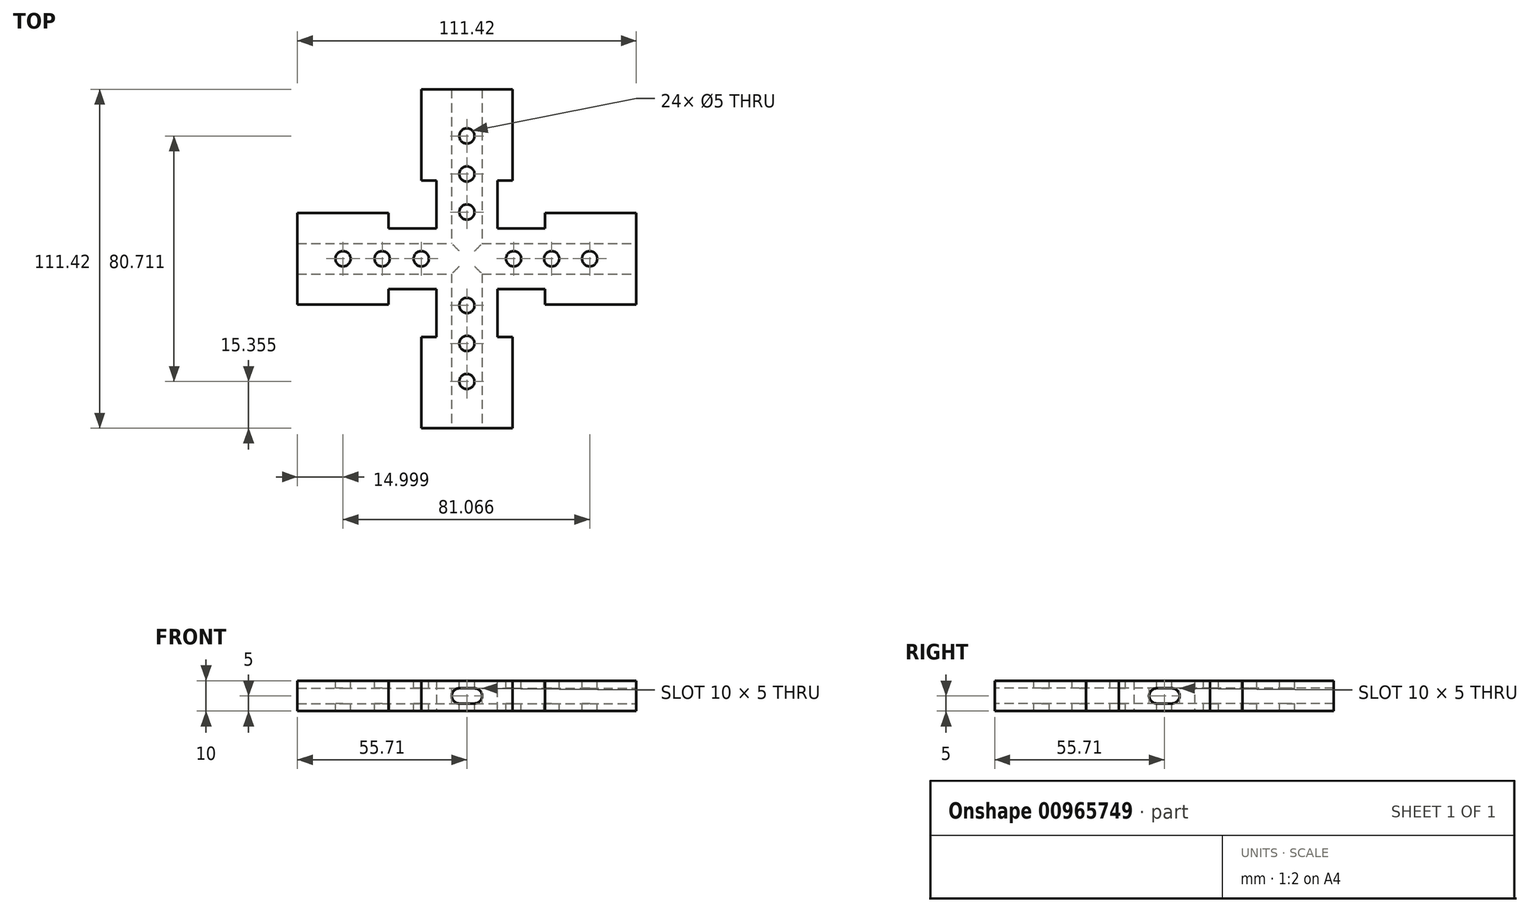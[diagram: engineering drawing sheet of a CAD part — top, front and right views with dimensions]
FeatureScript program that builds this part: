
annotation { "Feature Type Name" : "Feature", "Feature Type Description" : "" }
export const myFeature = defineFeature(function(context is Context, id is Id, definition is map)
    precondition{}
    {
        {
            var Q0;
            Q0=qCreatedBy(makeId("Top.planeOp"),FACE);
            var sketch = newSketch(context, id + "F0", { "sketchPlane" : qUnion([Q0])});
            skLineSegment(sketch, "E0.bottom", {"start": v(55.71, 10) * mm, "end": v(-55.71, 10) * mm});
            skLineSegment(sketch, "E0.top", {"start": v(55.71, -10) * mm, "end": v(-55.71, -10) * mm});
            skLineSegment(sketch, "E0.left", {"start": v(55.71, 10) * mm, "end": v(55.71, -10) * mm});
            skLineSegment(sketch, "E0.right", {"start": v(-55.71, 10) * mm, "end": v(-55.71, -10) * mm});
            skPoint(sketch, "E0.middle", {"position": v(0, 0) * mm});
            skLineSegment(sketch, "E1.bottom", {"start": v(10, 55.71) * mm, "end": v(-10, 55.71) * mm});
            skLineSegment(sketch, "E1.top", {"start": v(10, -55.71) * mm, "end": v(-10, -55.71) * mm});
            skLineSegment(sketch, "E1.left", {"start": v(10, 55.71) * mm, "end": v(10, -55.71) * mm});
            skLineSegment(sketch, "E1.right", {"start": v(-10, 55.71) * mm, "end": v(-10, -55.71) * mm});
            skSolve(sketch);
        }
        {
            var Q0;
            Q0 = qSketchRegion(id + "F0", true);
            extrude(context, id + "F1", {"entities" : qUnion([Q0]), "endBound" : BoundingType.SYMMETRIC, "depth" : 10 * mm, "offsetDistance" : 25 * mm});
        }
        {
            var Q0;
            Q0=makeQuery(id+"F1.opExtrude","SWEPT_FACE",FACE,{"disambiguationData":[OSD([sQuery(id+"F0.wireOp",EDGE,"E1.top")])]});
            var sketch = newSketch(context, id + "F2", { "sketchPlane" : qUnion([Q0])});
            skPoint(sketch, "E2.middle", {"position": v(0, 0) * mm});
            skArc(sketch, "E3", {"start": v(2.5, -2.5) * mm, "mid": v(5, 0) * mm, "end": v(2.5, 2.5) * mm});
            skArc(sketch, "E4", {"start": v(-2.5, 2.5) * mm, "mid": v(-5, 0) * mm, "end": v(-2.5, -2.5) * mm});
            skLineSegment(sketch, "E5", {"start": v(-2.5, 2.5) * mm, "end": v(2.5, 2.5) * mm});
            skLineSegment(sketch, "E6", {"start": v(-2.5, -2.5) * mm, "end": v(2.5, -2.5) * mm});
            skSolve(sketch);
        }
        {
            var Q0;
            Q0=makeQuery(id+"F1.opExtrude","SWEPT_FACE",FACE,{"disambiguationData":[OSD([sQuery(id+"F0.wireOp",EDGE,"E0.left")])]});
            var sketch = newSketch(context, id + "F3", { "sketchPlane" : qUnion([Q0])});
            skArc(sketch, "E7", {"start": v(2.5, -2.5) * mm, "mid": v(5, 0) * mm, "end": v(2.5, 2.5) * mm});
            skArc(sketch, "E8", {"start": v(-2.5, 2.5) * mm, "mid": v(-5, 0) * mm, "end": v(-2.5, -2.5) * mm});
            skLineSegment(sketch, "E9", {"start": v(-2.5, 2.5) * mm, "end": v(2.5, 2.5) * mm});
            skLineSegment(sketch, "E10", {"start": v(2.5, -2.5) * mm, "end": v(-2.5, -2.5) * mm});
            skPoint(sketch, "E11.center.orphan", {"position": v(0, 0) * mm});
            skSolve(sketch);
        }
        {
            var Q0;
            Q0 = qSketchRegion(id + "F2", true);
            extrude(context, id + "F4", {"entities" : qUnion([Q0]), "operationType" : NewBodyOperationType.REMOVE, "oppositeDirection" : true, "depth" : 120 * mm, "offsetDistance" : 25 * mm});
        }
        {
            var Q0;
            {var subQ0=sQuery(id+"F0.wireOp",EDGE,"E1.left");Q0=makeQuery(id+"F1.opExtrude","SWEPT_FACE",FACE,{"disambiguationData":[OSD([subQ0]),TDD([makeQuery(id+"F0.imprint","IMPRINT",EDGE,{"disambiguationData":[TD([[makeQuery(id+"F0.imprint","INTERSECT",VERTEX,{"derivedFrom":[sQuery(id+"F0.wireOp",EDGE,"E1.top"),subQ0]}),1.0]])],"derivedFrom":subQ0})])]});}
            var sketch = newSketch(context, id + "F5", { "sketchPlane" : qUnion([Q0])});
            skLineSegment(sketch, "E12", {"start": v(-55.71, 0) * mm, "end": v(-40.71, 0) * mm});
            skLineSegment(sketch, "E13.bottom", {"start": v(-55.71, 5) * mm, "end": v(-25.71, 5) * mm});
            skLineSegment(sketch, "E13.top", {"start": v(-55.71, -5) * mm, "end": v(-25.71, -5) * mm});
            skLineSegment(sketch, "E13.left", {"start": v(-55.71, 5) * mm, "end": v(-55.71, -5) * mm});
            skLineSegment(sketch, "E13.right", {"start": v(-25.71, 5) * mm, "end": v(-25.71, -5) * mm});
            skPoint(sketch, "E13.middle", {"position": v(-40.71, 0) * mm});
            skSolve(sketch);
        }
        {
            var Q0;
            Q0 = qSketchRegion(id + "F5", true);
            extrude(context, id + "F6", {"entities" : qUnion([Q0]), "operationType" : NewBodyOperationType.ADD, "depth" : 5 * mm, "offsetDistance" : 25 * mm, "hasSecondDirection" : true, "secondDirectionOppositeDirection" : true, "secondDirectionDepth" : 25 * mm});
        }
        {
            var Q0;
            {var subQ0=sQuery(id+"F0.wireOp",EDGE,"E1.right");Q0=makeQuery(id+"F1.opExtrude","SWEPT_FACE",FACE,{"disambiguationData":[OSD([subQ0]),TDD([makeQuery(id+"F0.imprint","IMPRINT",EDGE,{"disambiguationData":[TD([[makeQuery(id+"F0.imprint","INTERSECT",VERTEX,{"derivedFrom":[sQuery(id+"F0.wireOp",EDGE,"E1.bottom"),subQ0]}),-1.0]])],"derivedFrom":subQ0})])]});}
            var sketch = newSketch(context, id + "F7", { "sketchPlane" : qUnion([Q0])});
            skLineSegment(sketch, "E14.bottom", {"start": v(-55.71, 5) * mm, "end": v(-25.71, 5) * mm});
            skLineSegment(sketch, "E14.top", {"start": v(-55.71, -5) * mm, "end": v(-25.71, -5) * mm});
            skLineSegment(sketch, "E14.left", {"start": v(-55.71, 5) * mm, "end": v(-55.71, -5) * mm});
            skLineSegment(sketch, "E14.right", {"start": v(-25.71, 5) * mm, "end": v(-25.71, -5) * mm});
            skPoint(sketch, "E14.middle", {"position": v(-40.71, 0) * mm});
            skSolve(sketch);
        }
        {
            var Q0;
            Q0 = qSketchRegion(id + "F7", true);
            extrude(context, id + "F8", {"entities" : qUnion([Q0]), "operationType" : NewBodyOperationType.ADD, "depth" : 5 * mm, "offsetDistance" : 25 * mm, "hasSecondDirection" : true, "secondDirectionOppositeDirection" : true, "secondDirectionDepth" : 25 * mm});
        }
        {
            var Q0;
            {var subQ0=sQuery(id+"F0.wireOp",EDGE,"E0.bottom");Q0=makeQuery(id+"F1.opExtrude","SWEPT_FACE",FACE,{"disambiguationData":[OSD([subQ0]),TDD([makeQuery(id+"F0.imprint","IMPRINT",EDGE,{"disambiguationData":[TD([[makeQuery(id+"F0.imprint","INTERSECT",VERTEX,{"derivedFrom":[subQ0,sQuery(id+"F0.wireOp",EDGE,"E0.left")]}),-1.0]])],"derivedFrom":subQ0})])]});}
            var sketch = newSketch(context, id + "F9", { "sketchPlane" : qUnion([Q0])});
            skPoint(sketch, "E15.middle", {"position": v(-30.71, 0) * mm});
            skLineSegment(sketch, "E16.bottom", {"start": v(-55.71, 5) * mm, "end": v(-25.71, 5) * mm});
            skLineSegment(sketch, "E16.top", {"start": v(-55.71, -5) * mm, "end": v(-25.71, -5) * mm});
            skLineSegment(sketch, "E16.left", {"start": v(-55.71, 5) * mm, "end": v(-55.71, -5) * mm});
            skLineSegment(sketch, "E16.right", {"start": v(-25.71, 5) * mm, "end": v(-25.71, -5) * mm});
            skPoint(sketch, "E16.middle", {"position": v(-40.71, 0) * mm});
            skSolve(sketch);
        }
        {
            var Q0;
            Q0 = qSketchRegion(id + "F9", true);
            extrude(context, id + "F10", {"entities" : qUnion([Q0]), "operationType" : NewBodyOperationType.ADD, "depth" : 5 * mm, "offsetDistance" : 25 * mm, "hasSecondDirection" : true, "secondDirectionOppositeDirection" : true, "secondDirectionDepth" : 25 * mm});
        }
        {
            var Q0;
            {var subQ0=sQuery(id+"F0.wireOp",EDGE,"E0.bottom");Q0=makeQuery(id+"F1.opExtrude","SWEPT_FACE",FACE,{"disambiguationData":[OSD([subQ0]),TDD([makeQuery(id+"F0.imprint","IMPRINT",EDGE,{"disambiguationData":[TD([[makeQuery(id+"F0.imprint","INTERSECT",VERTEX,{"derivedFrom":[subQ0,sQuery(id+"F0.wireOp",EDGE,"E0.right")]}),1.0]])],"derivedFrom":subQ0})])]});}
            var sketch = newSketch(context, id + "F11", { "sketchPlane" : qUnion([Q0])});
            skLineSegment(sketch, "E17.bottom", {"start": v(55.71, 5) * mm, "end": v(25.71, 5) * mm});
            skLineSegment(sketch, "E17.top", {"start": v(55.71, -5) * mm, "end": v(25.71, -5) * mm});
            skLineSegment(sketch, "E17.left", {"start": v(55.71, 5) * mm, "end": v(55.71, -5) * mm});
            skLineSegment(sketch, "E17.right", {"start": v(25.71, 5) * mm, "end": v(25.71, -5) * mm});
            skSolve(sketch);
        }
        {
            var Q0;
            Q0 = qSketchRegion(id + "F11", true);
            extrude(context, id + "F12", {"entities" : qUnion([Q0]), "operationType" : NewBodyOperationType.ADD, "depth" : 5 * mm, "offsetDistance" : 25 * mm, "hasSecondDirection" : true, "secondDirectionOppositeDirection" : true, "secondDirectionDepth" : 25 * mm});
        }
        {
            var Q0;
            Q0=makeQuery(id+"F12.boolean.opBoolean","MERGE",FACE,{"derivedFrom":[makeQuery(id+"F10.boolean.opBoolean","MERGE",FACE,{"derivedFrom":[makeQuery(id+"F8.boolean.opBoolean","MERGE",FACE,{"derivedFrom":[makeQuery(id+"F6.boolean.opBoolean","MERGE",FACE,{"derivedFrom":[makeQuery(id+"F1.opExtrude","CAP_FACE",FACE,{"disambiguationData":[OSD([sQuery(id+"F0.wireOp",EDGE,"E0.bottom"),sQuery(id+"F0.wireOp",EDGE,"E0.top"),sQuery(id+"F0.wireOp",EDGE,"E0.left"),sQuery(id+"F0.wireOp",EDGE,"E0.right"),sQuery(id+"F0.wireOp",EDGE,"E1.bottom"),sQuery(id+"F0.wireOp",EDGE,"E1.top"),sQuery(id+"F0.wireOp",EDGE,"E1.left"),sQuery(id+"F0.wireOp",EDGE,"E1.right")])],"isStart":false}),makeQuery(id+"F6.opExtrude","SWEPT_FACE",FACE,{"disambiguationData":[OSD([sQuery(id+"F5.wireOp",EDGE,"piaZW8z0-ljMb-9kP3-zudl-aKQeHL9OJzn6.bottom")])]})]}),makeQuery(id+"F8.opExtrude","SWEPT_FACE",FACE,{"disambiguationData":[OSD([sQuery(id+"F7.wireOp",EDGE,"WXLkNF3s-gk87-DAri-4asK-DUwRPPsIz8zQ.bottom")])]})]}),makeQuery(id+"F10.opExtrude","SWEPT_FACE",FACE,{"disambiguationData":[OSD([sQuery(id+"F9.wireOp",EDGE,"E15.bottom")])]})]}),makeQuery(id+"F12.opExtrude","SWEPT_FACE",FACE,{"disambiguationData":[OSD([sQuery(id+"F11.wireOp",EDGE,"4IJIhBuP-4uAV-hZB2-eqjq-57dkDs7jMEwz.bottom")])]})]});
            var sketch = newSketch(context, id + "F13", { "sketchPlane" : qUnion([Q0])});
            skCircle(sketch, "E18", {"center": v(-27.86, 0) * mm, "radius": 2.5 * mm});
            skCircle(sketch, "E19", {"center": v(-15, 0) * mm, "radius": 2.5 * mm});
            skCircle(sketch, "E20", {"center": v(-40.71, 0) * mm, "radius": 2.5 * mm});
            skCircle(sketch, "E21", {"center": v(27.86, 0) * mm, "radius": 2.5 * mm});
            skCircle(sketch, "E22", {"center": v(40.36, 0) * mm, "radius": 2.5 * mm});
            skCircle(sketch, "E23", {"center": v(15.36, 0) * mm, "radius": 2.5 * mm});
            skCircle(sketch, "E24", {"center": v(0, 27.86) * mm, "radius": 2.5 * mm});
            skCircle(sketch, "E25", {"center": v(0, 40.36) * mm, "radius": 2.5 * mm});
            skCircle(sketch, "E26", {"center": v(0, 15.36) * mm, "radius": 2.5 * mm});
            skCircle(sketch, "E27", {"center": v(0, -27.86) * mm, "radius": 2.5 * mm});
            skCircle(sketch, "E28", {"center": v(0, -15.36) * mm, "radius": 2.5 * mm});
            skCircle(sketch, "E29", {"center": v(0, -40.36) * mm, "radius": 2.5 * mm});
            skSolve(sketch);
        }
        {
            var Q0;
            Q0 = qSketchRegion(id + "F13", true);
            extrude(context, id + "F14", {"entities" : qUnion([Q0]), "operationType" : NewBodyOperationType.REMOVE, "oppositeDirection" : true, "depth" : 10 * mm, "offsetDistance" : 25 * mm});
        }
        {
            var Q0;
            Q0 = qSketchRegion(id + "F2", true);
            extrude(context, id + "F15", {"entities" : qUnion([Q0]), "operationType" : NewBodyOperationType.REMOVE, "oppositeDirection" : true, "depth" : 116.7 * mm, "offsetDistance" : 25 * mm});
        }
        {
            var Q0;
            Q0 = qSketchRegion(id + "F3", true);
            extrude(context, id + "F16", {"entities" : qUnion([Q0]), "operationType" : NewBodyOperationType.REMOVE, "oppositeDirection" : true, "depth" : 135 * mm, "offsetDistance" : 25 * mm});
        }
    });
